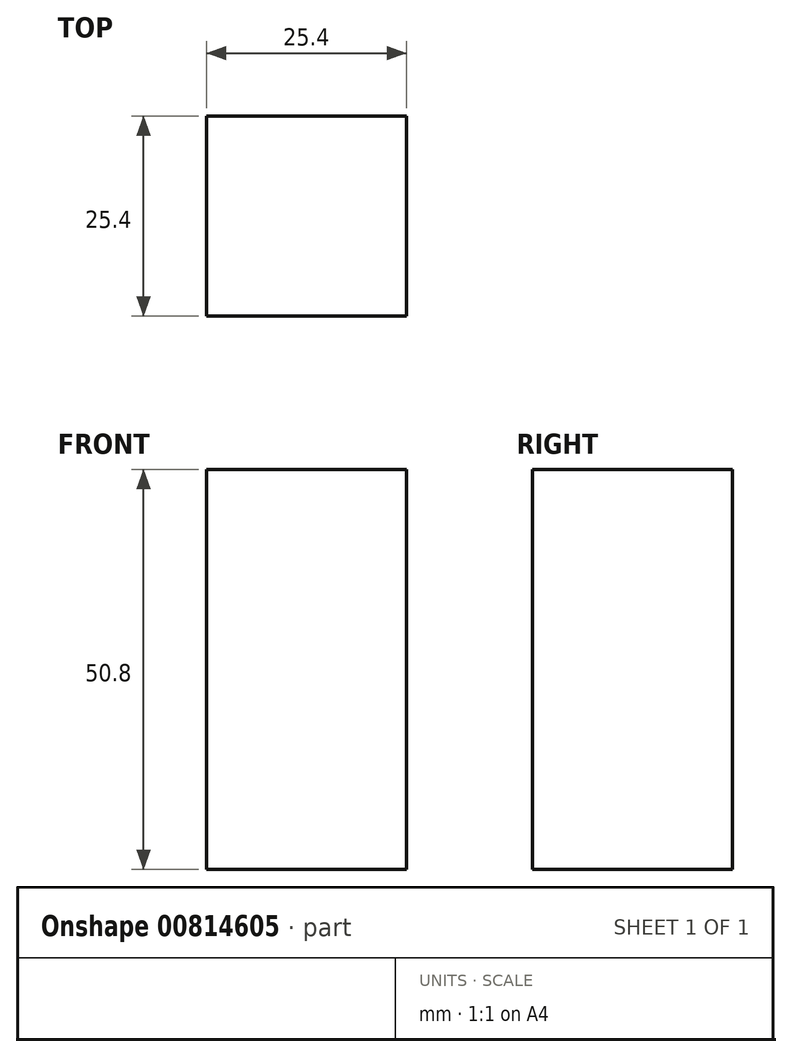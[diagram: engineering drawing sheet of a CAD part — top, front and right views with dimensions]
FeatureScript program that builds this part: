
annotation { "Feature Type Name" : "Feature", "Feature Type Description" : "" }
export const myFeature = defineFeature(function(context is Context, id is Id, definition is map)
    precondition{}
    {
        {
            var Q0;
            Q0=qCreatedBy(makeId("Front.planeOp"),FACE);
            var sketch = newSketch(context, id + "F0", { "sketchPlane" : qUnion([Q0])});
            skLineSegment(sketch, "E0", {"start": v(-43.73, 61.31) * mm, "end": v(-18.33, 61.31) * mm});
            skLineSegment(sketch, "E1", {"start": v(-18.33, 61.31) * mm, "end": v(-18.33, 10.5) * mm});
            skLineSegment(sketch, "E2", {"start": v(-18.33, 10.5) * mm, "end": v(-43.72, 10.5) * mm});
            skLineSegment(sketch, "E3", {"start": v(-43.72, 10.5) * mm, "end": v(-43.73, 61.31) * mm});
            skSolve(sketch);
        }
        {
            var Q0;
            Q0 = qSketchRegion(id + "F0", true);
            extrude(context, id + "F1", {"entities" : qUnion([Q0]), "depth" : 25.4 * mm, "offsetDistance" : 25.4 * mm});
        }
    });
